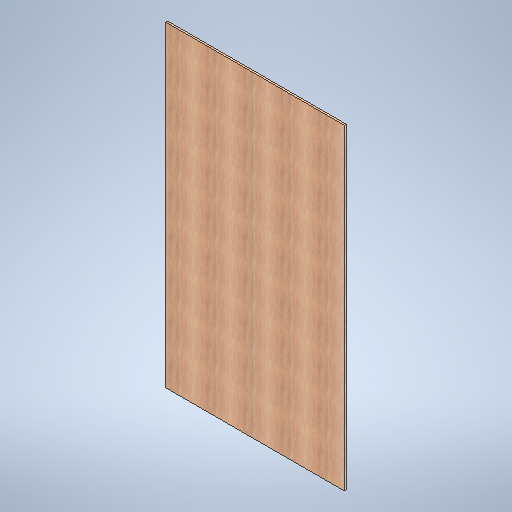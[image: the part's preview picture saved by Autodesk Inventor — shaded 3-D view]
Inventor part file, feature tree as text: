
AUTODESK INVENTOR PART (.ipt)
format: ipt  version: 2025.1 (Build 291241020, 241B)  size: 358,912 bytes
history: native  units: in
note: dims shown in document units (in); Inventor stores cm internally (conversion verified against a paired STEP export)
features: extrude x1, sketch x1
ambient origin geometry x8: Origin, YZ Plane, XZ Plane, XY Plane, X Axis, Y Axis, Z Axis, Center Point
bodies: Solid1 (feature_tree)
feature tree (2):
  extrude  "Extrusion1"  Depth=48.0in
  sketch  "Sketch1"  dims[d2=85.0in d3=48.0in d4=0.5in d5=0.0in]
